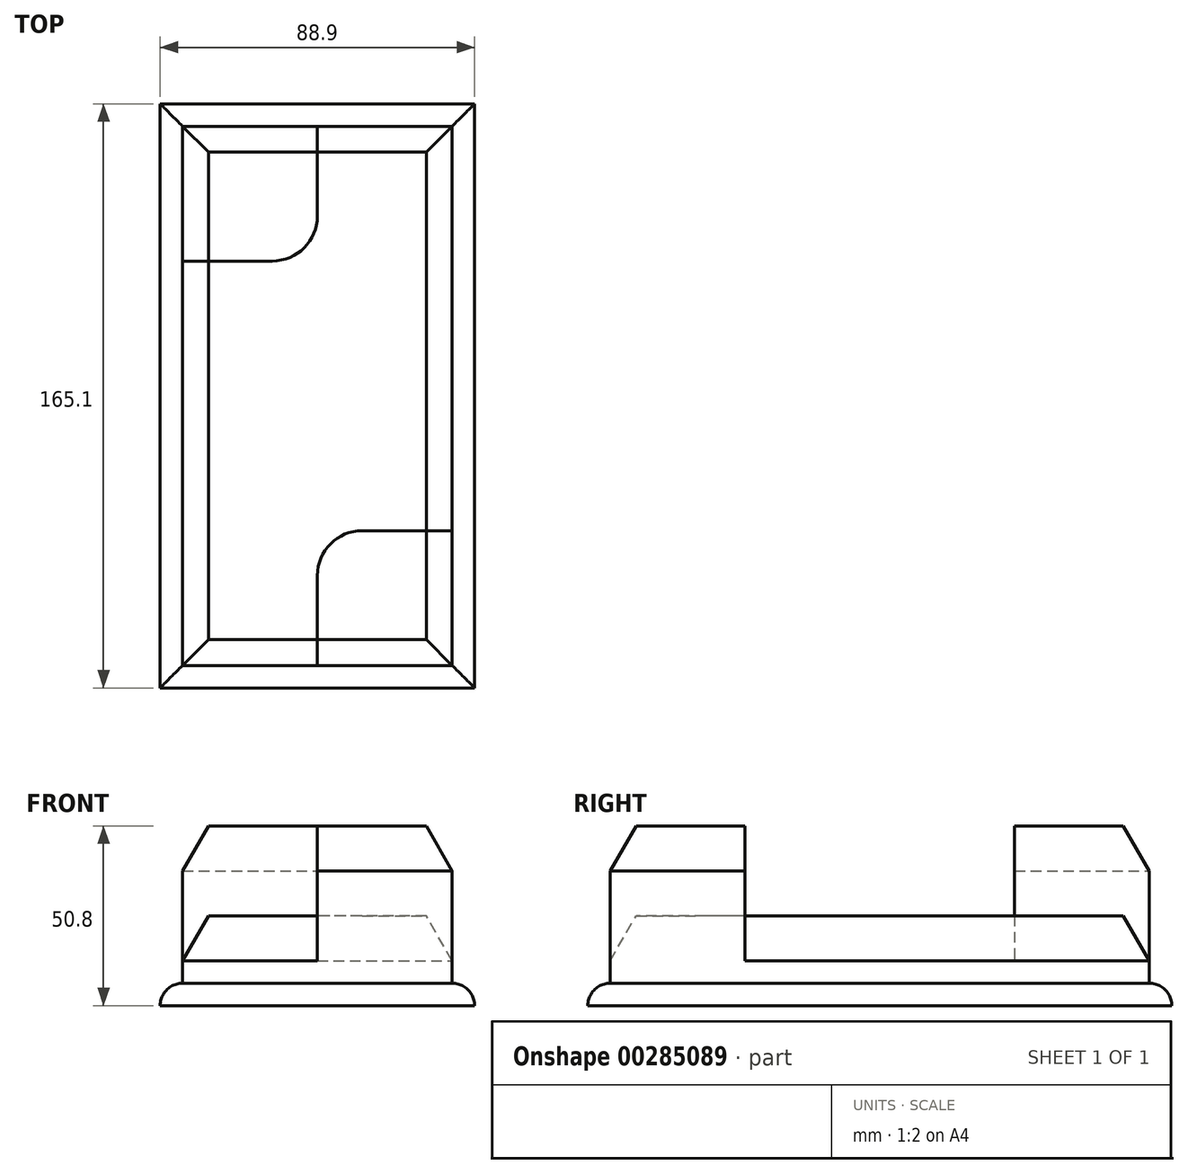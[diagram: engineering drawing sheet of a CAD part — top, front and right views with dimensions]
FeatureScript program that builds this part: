
annotation { "Feature Type Name" : "Feature", "Feature Type Description" : "" }
export const myFeature = defineFeature(function(context is Context, id is Id, definition is map)
    precondition{}
    {
        {
            var Q0;
            Q0=qCreatedBy(makeId("Top.planeOp"),FACE);
            var sketch = newSketch(context, id + "F0", { "sketchPlane" : qUnion([Q0])});
            skLineSegment(sketch, "E0.bottom", {"start": v(38.1, -76.2) * mm, "end": v(-38.1, -76.2) * mm});
            skLineSegment(sketch, "E0.top", {"start": v(38.1, 76.2) * mm, "end": v(-38.1, 76.2) * mm});
            skLineSegment(sketch, "E0.left", {"start": v(38.1, -76.2) * mm, "end": v(38.1, 76.2) * mm});
            skLineSegment(sketch, "E0.right", {"start": v(-38.1, -76.2) * mm, "end": v(-38.1, 76.2) * mm});
            skPoint(sketch, "E0.middle", {"position": v(0, 0) * mm});
            skLineSegment(sketch, "E1.bottom", {"start": v(44.45, -82.55) * mm, "end": v(-44.45, -82.55) * mm});
            skLineSegment(sketch, "E1.top", {"start": v(44.45, 82.55) * mm, "end": v(-44.45, 82.55) * mm});
            skLineSegment(sketch, "E1.left", {"start": v(44.45, -82.55) * mm, "end": v(44.45, 82.55) * mm});
            skLineSegment(sketch, "E1.right", {"start": v(-44.45, -82.55) * mm, "end": v(-44.45, 82.55) * mm});
            skLineSegment(sketch, "E2.top", {"start": v(-38.1, 38.1) * mm, "end": v(-12.7, 38.1) * mm});
            skLineSegment(sketch, "E2.right", {"start": v(0, 76.2) * mm, "end": v(0, 50.8) * mm});
            skPoint(sketch, "E3.visualSharp", {"position": v(0, 38.1) * mm});
            skArc(sketch, "E3.filletArc", {"start": v(-12.7, 38.1) * mm, "mid": v(-3.72, 41.82) * mm, "end": v(0, 50.8) * mm});
            skPoint(sketch, "E4.visualSharp", {"position": v(0, -38.1) * mm});
            skLineSegment(sketch, "E5", {"start": v(0, -76.2) * mm, "end": v(0, -50.8) * mm});
            skLineSegment(sketch, "E6", {"start": v(12.7, -38.1) * mm, "end": v(38.1, -38.1) * mm});
            skArc(sketch, "E7.filletArc", {"start": v(12.7, -38.1) * mm, "mid": v(3.72, -41.82) * mm, "end": v(0, -50.8) * mm});
            skSolve(sketch);
        }
        {
            var Q0;
            Q0=makeQuery(id+"F0.imprint","IMPRINT",FACE,{"disambiguationData":[TD([[makeQuery(id+"F0.imprint","IMPRINT",EDGE,{"derivedFrom":sQuery(id+"F0.wireOp",EDGE,"E1.bottom")}),-1.0]])]});
            extrude(context, id + "F1", {"entities" : qUnion([Q0]), "depth" : 6.35 * mm});
        }
        {
            var Q0;
            {var subQ0=sQuery(id+"F0.wireOp",EDGE,"E2.top");Q0=makeQuery(id+"F0.imprint","IMPRINT",FACE,{"disambiguationData":[TD([[makeQuery(id+"F0.imprint","IMPRINT",EDGE,{"derivedFrom":subQ0}),1.0]])]});}
            var Q1;
            {var subQ4=sQuery(id+"F0.wireOp",EDGE,"E5");Q1=makeQuery(id+"F0.imprint","IMPRINT",FACE,{"disambiguationData":[TD([[makeQuery(id+"F0.imprint","IMPRINT",EDGE,{"derivedFrom":subQ4}),-1.0]])]});}
            extrude(context, id + "F2", {"entities" : qUnion([Q0, Q1]), "operationType" : NewBodyOperationType.ADD, "depth" : 50.8 * mm});
        }
        {
            var Q0;
            {var subQ8=sQuery(id+"F0.wireOp",EDGE,"E2.top");Q0=makeQuery(id+"F0.imprint","IMPRINT",FACE,{"disambiguationData":[TD([[makeQuery(id+"F0.imprint","IMPRINT",EDGE,{"derivedFrom":subQ8}),-1.0]])]});}
            extrude(context, id + "F3", {"entities" : qUnion([Q0]), "operationType" : NewBodyOperationType.ADD, "depth" : 25.4 * mm});
        }
        {
            var Q0;
            Q0=makeQuery(id+"F1.opExtrude","CAP_EDGE",EDGE,{"disambiguationData":[OSD([sQuery(id+"F0.wireOp",EDGE,"E1.bottom")])],"isStart":false});
            var Q1;
            Q1=makeQuery(id+"F1.opExtrude","CAP_EDGE",EDGE,{"disambiguationData":[OSD([sQuery(id+"F0.wireOp",EDGE,"E1.right")])],"isStart":false});
            var Q2;
            Q2=makeQuery(id+"F1.opExtrude","CAP_EDGE",EDGE,{"disambiguationData":[OSD([sQuery(id+"F0.wireOp",EDGE,"E1.top")])],"isStart":false});
            var Q3;
            Q3=makeQuery(id+"F1.opExtrude","CAP_EDGE",EDGE,{"disambiguationData":[OSD([sQuery(id+"F0.wireOp",EDGE,"E1.left")])],"isStart":false});
            fillet(context, id + "F4", {"entities" : qUnion([Q0, Q1, Q2, Q3]), "radius" : 6.35 * mm, "tangentPropagation" : true, "allowEdgeOverflow" : false});
        }
        {
            var Q0;
            Q0=makeQuery(id+"F2.opExtrude","CAP_EDGE",EDGE,{"disambiguationData":[OSD([sQuery(id+"F0.wireOp",EDGE,"E0.top")])],"isStart":false});
            var Q1;
            Q1=makeQuery(id+"F2.opExtrude","CAP_EDGE",EDGE,{"disambiguationData":[OSD([sQuery(id+"F0.wireOp",EDGE,"E0.right")])],"isStart":false});
            var Q2;
            Q2=makeQuery(id+"F2.opExtrude","CAP_EDGE",EDGE,{"disambiguationData":[OSD([sQuery(id+"F0.wireOp",EDGE,"E0.left")])],"isStart":false});
            var Q3;
            Q3=makeQuery(id+"F3.opExtrude","CAP_EDGE",EDGE,{"disambiguationData":[OSD([sQuery(id+"F0.wireOp",EDGE,"E0.left")])],"isStart":false});
            var Q4;
            Q4=makeQuery(id+"F3.opExtrude","CAP_EDGE",EDGE,{"disambiguationData":[OSD([sQuery(id+"F0.wireOp",EDGE,"E0.top")])],"isStart":false});
            chamfer(context, id + "F5", {"entities" : qUnion([Q0, Q1, Q2, Q3, Q4]), "chamferType" : ChamferType.OFFSET_ANGLE, "width" : 12.7 * mm, "oppositeDirection" : true, "angle" : 30 * degree, "tangentPropagation" : true});
        }
        {
            var Q0;
            Q0=makeQuery(id+"F2.opExtrude","CAP_EDGE",EDGE,{"disambiguationData":[OSD([sQuery(id+"F0.wireOp",EDGE,"E0.bottom")])],"isStart":false});
            var Q1;
            Q1=makeQuery(id+"F3.opExtrude","CAP_EDGE",EDGE,{"disambiguationData":[OSD([sQuery(id+"F0.wireOp",EDGE,"E0.right")])],"isStart":false});
            var Q2;
            Q2=makeQuery(id+"F3.opExtrude","CAP_EDGE",EDGE,{"disambiguationData":[OSD([sQuery(id+"F0.wireOp",EDGE,"E0.bottom")])],"isStart":false});
            chamfer(context, id + "F6", {"entities" : qUnion([Q0, Q1, Q2]), "chamferType" : ChamferType.OFFSET_ANGLE, "width" : 12.7 * mm, "oppositeDirection" : false, "angle" : 30 * degree, "tangentPropagation" : true});
        }
    });
